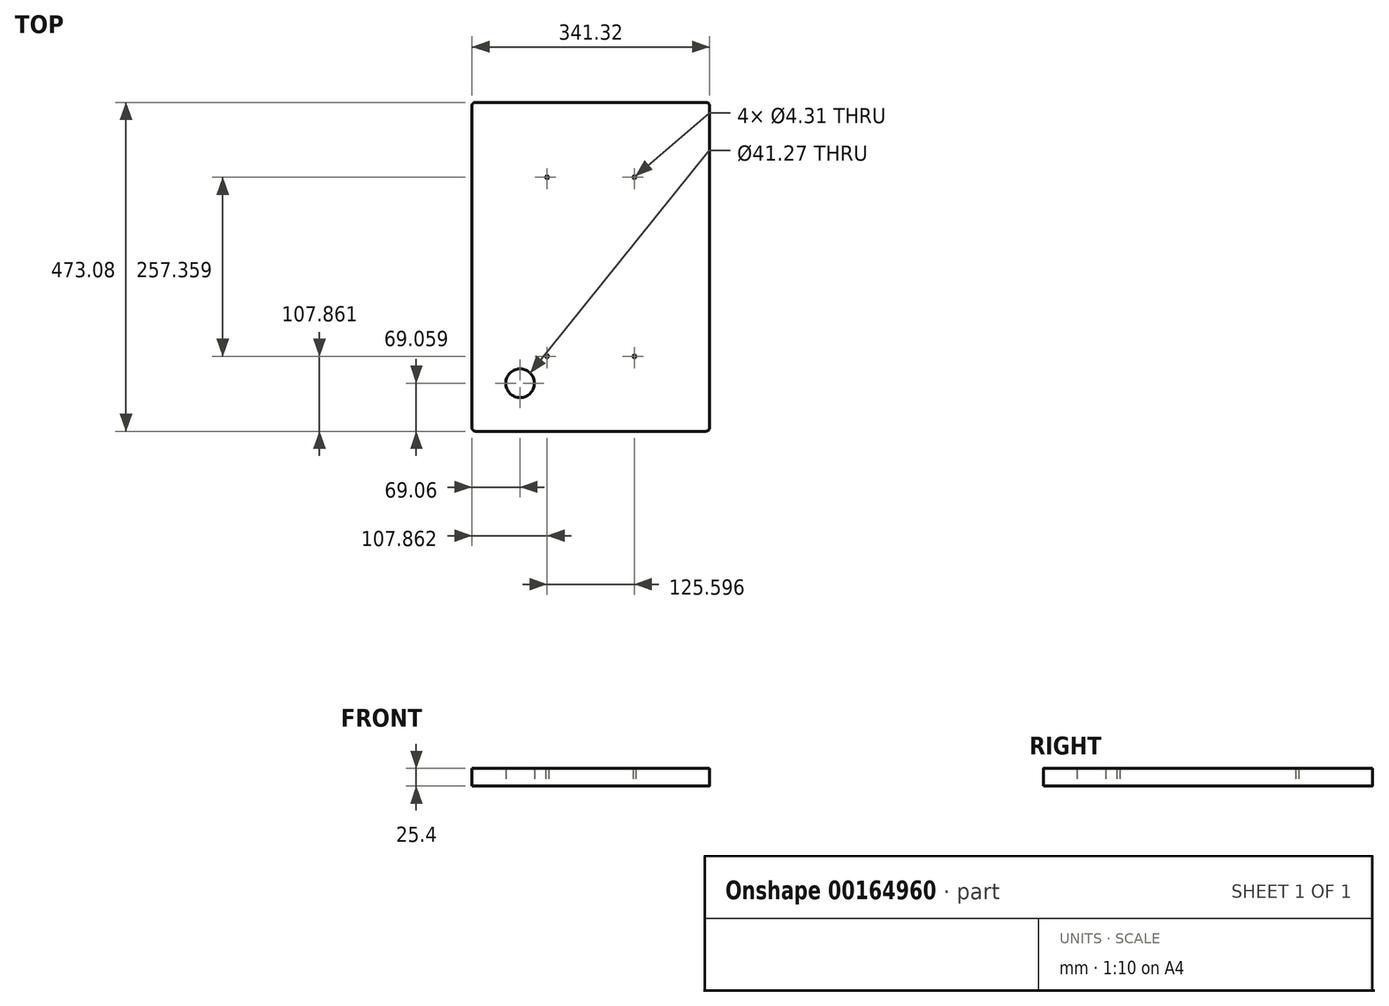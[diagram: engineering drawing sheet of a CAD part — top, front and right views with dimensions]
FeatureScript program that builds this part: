
annotation { "Feature Type Name" : "Feature", "Feature Type Description" : "" }
export const myFeature = defineFeature(function(context is Context, id is Id, definition is map)
    precondition{}
    {
        {
            var Q0;
            Q0=qCreatedBy(makeId("Top.planeOp"),FACE);
            var sketch = newSketch(context, id + "F0", { "sketchPlane" : qUnion([Q0])});
            skLineSegment(sketch, "E0.bottom", {"start": v(170.66, 236.54) * mm, "end": v(-170.66, 236.54) * mm});
            skLineSegment(sketch, "E0.top", {"start": v(170.66, -236.54) * mm, "end": v(-170.66, -236.54) * mm});
            skLineSegment(sketch, "E0.left", {"start": v(170.66, 236.54) * mm, "end": v(170.66, -236.54) * mm});
            skLineSegment(sketch, "E0.right", {"start": v(-170.66, 236.54) * mm, "end": v(-170.66, -236.54) * mm});
            skPoint(sketch, "E0.middle", {"position": v(0, 0) * mm});
            skLineSegment(sketch, "E1.bottom", {"start": v(62.8, 128.68) * mm, "end": v(-62.8, 128.68) * mm, "construction": true});
            skLineSegment(sketch, "E1.top", {"start": v(62.8, -128.68) * mm, "end": v(-62.8, -128.68) * mm, "construction": true});
            skLineSegment(sketch, "E1.left", {"start": v(62.8, 128.68) * mm, "end": v(62.8, -128.68) * mm, "construction": true});
            skLineSegment(sketch, "E1.right", {"start": v(-62.8, 128.68) * mm, "end": v(-62.8, -128.68) * mm, "construction": true});
            skLineSegment(sketch, "E2", {"start": v(62.8, 128.68) * mm, "end": v(62.8, 236.54) * mm, "construction": true});
            skLineSegment(sketch, "E3", {"start": v(62.8, 128.68) * mm, "end": v(170.66, 128.68) * mm, "construction": true});
            skCircle(sketch, "E4", {"center": v(62.8, 128.68) * mm, "radius": 2.15 * mm});
            skCircle(sketch, "E5", {"center": v(-62.8, 128.68) * mm, "radius": 2.15 * mm});
            skCircle(sketch, "E6", {"center": v(62.8, -128.68) * mm, "radius": 2.15 * mm});
            skCircle(sketch, "E7", {"center": v(-62.8, -128.68) * mm, "radius": 2.15 * mm});
            skLineSegment(sketch, "E8", {"start": v(-101.6, 0) * mm, "end": v(0, 0) * mm, "construction": true});
            skLineSegment(sketch, "E9", {"start": v(-101.6, 0) * mm, "end": v(-101.6, -167.48) * mm, "construction": true});
            skCircle(sketch, "E10", {"center": v(-101.6, -167.48) * mm, "radius": 20.64 * mm});
            skSolve(sketch);
        }
        {
            var Q0;
            Q0 = qSketchRegion(id + "F0", true);
            extrude(context, id + "F1", {"entities" : qUnion([Q0]), "depth" : 25.4 * mm});
        }
        {
            var Q0;
            Q0=makeQuery(id+"F1.opExtrude","SWEPT_EDGE",EDGE,{"disambiguationData":[OSD([sQuery(id+"F0.wireOp",EDGE,"E0.bottom"),sQuery(id+"F0.wireOp",EDGE,"E0.right")])]});
            var Q1;
            Q1=makeQuery(id+"F1.opExtrude","SWEPT_EDGE",EDGE,{"disambiguationData":[OSD([sQuery(id+"F0.wireOp",EDGE,"E0.bottom"),sQuery(id+"F0.wireOp",EDGE,"E0.left")])]});
            var Q2;
            Q2=makeQuery(id+"F1.opExtrude","SWEPT_EDGE",EDGE,{"disambiguationData":[OSD([sQuery(id+"F0.wireOp",EDGE,"E0.top"),sQuery(id+"F0.wireOp",EDGE,"E0.left")])]});
            var Q3;
            Q3=makeQuery(id+"F1.opExtrude","SWEPT_EDGE",EDGE,{"disambiguationData":[OSD([sQuery(id+"F0.wireOp",EDGE,"E0.top"),sQuery(id+"F0.wireOp",EDGE,"E0.right")])]});
            fillet(context, id + "F2", {"entities" : qUnion([Q0, Q1, Q2, Q3]), "radius" : 4.76 * mm, "tangentPropagation" : true, "allowEdgeOverflow" : false});
        }
    });
